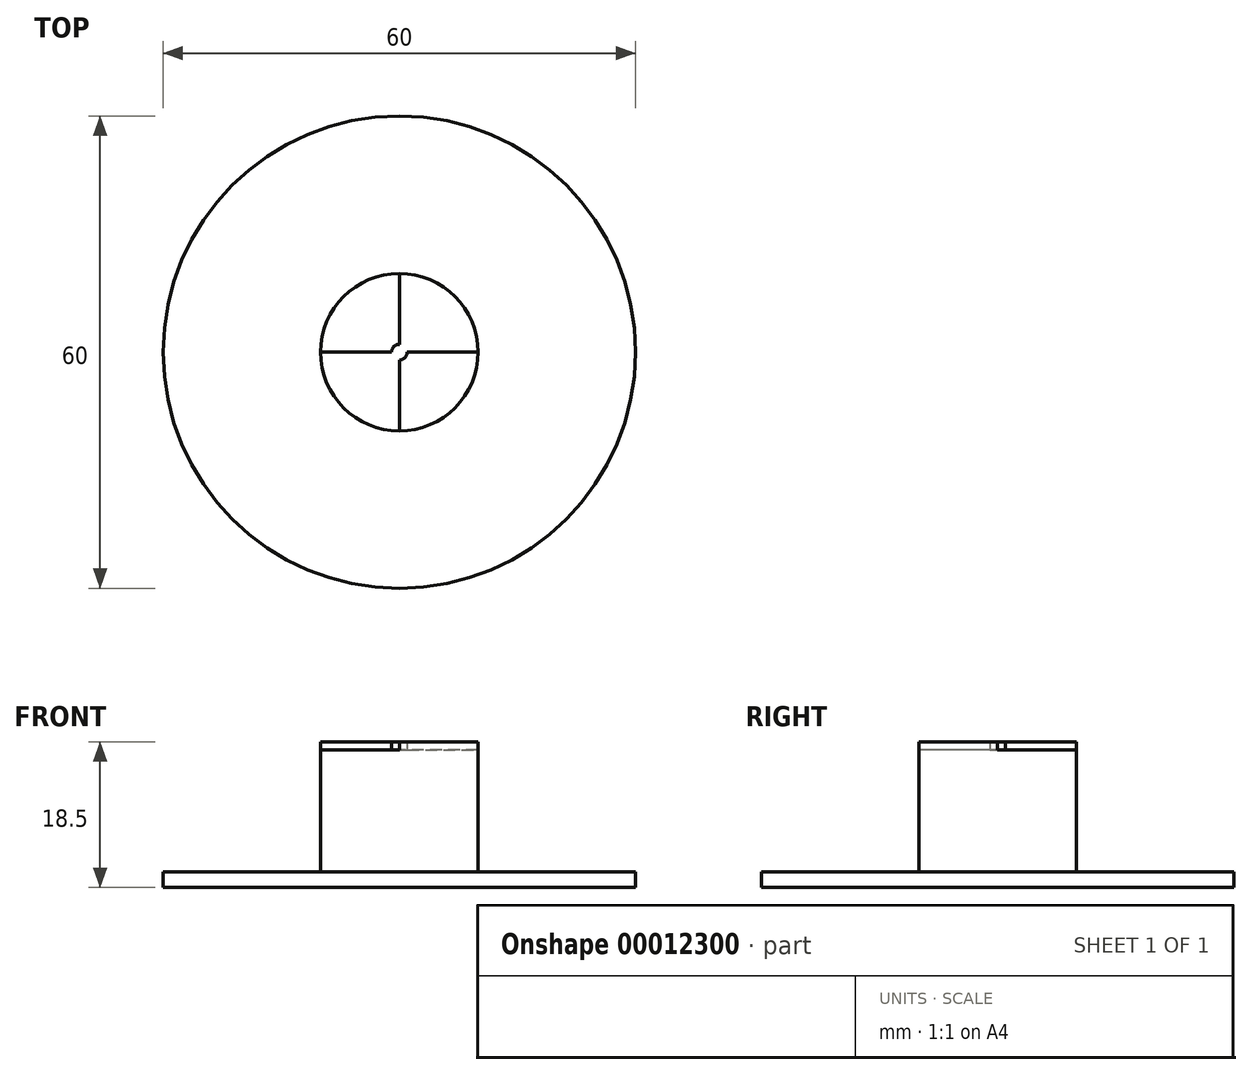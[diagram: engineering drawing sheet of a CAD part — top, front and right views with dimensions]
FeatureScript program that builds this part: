
annotation { "Feature Type Name" : "Feature", "Feature Type Description" : "" }
export const myFeature = defineFeature(function(context is Context, id is Id, definition is map)
    precondition{}
    {
        {
            var Q0;
            Q0=qCreatedBy(makeId("Top.planeOp"),FACE);
            var sketch = newSketch(context, id + "F0", { "sketchPlane" : qUnion([Q0])});
            skCircle(sketch, "E0", {"center": v(0, 0) * mm, "radius": 30 * mm});
            skSolve(sketch);
        }
        {
            var Q0;
            Q0=makeQuery(id+"F0.imprint","IMPRINT",FACE,{"disambiguationData":[TD([[makeQuery(id+"F0.imprint","IMPRINT",EDGE,{"derivedFrom":sQuery(id+"F0.wireOp",EDGE,"E0")}),1.0]])]});
            extrude(context, id + "F1", {"entities" : qUnion([Q0]), "depth" : 2 * mm});
        }
        {
            var Q0;
            Q0=makeQuery(id+"F1.opExtrude","CAP_FACE",FACE,{"disambiguationData":[OSD([sQuery(id+"F0.wireOp",EDGE,"E0")])],"isStart":false});
            var sketch = newSketch(context, id + "F2", { "sketchPlane" : qUnion([Q0])});
            skCircle(sketch, "E1", {"center": v(0, 0) * mm, "radius": 10 * mm});
            skSolve(sketch);
        }
        {
            var Q0;
            Q0=makeQuery(id+"F2.imprint","IMPRINT",FACE,{"disambiguationData":[TD([[makeQuery(id+"F2.imprint","IMPRINT",EDGE,{"derivedFrom":sQuery(id+"F2.wireOp",EDGE,"E1")}),1.0]])]});
            extrude(context, id + "F3", {"entities" : qUnion([Q0]), "operationType" : NewBodyOperationType.ADD, "depth" : 15.5 * mm});
        }
        {
            var Q0;
            Q0=makeQuery(id+"F3.opExtrude","CAP_FACE",FACE,{"disambiguationData":[OSD([sQuery(id+"F2.wireOp",EDGE,"E1")])],"isStart":false});
            var sketch = newSketch(context, id + "F4", { "sketchPlane" : qUnion([Q0])});
            skLineSegment(sketch, "E2", {"start": v(0, 0) * mm, "end": v(0, 10) * mm});
            skLineSegment(sketch, "E3", {"start": v(0, 0) * mm, "end": v(0, -10) * mm});
            skLineSegment(sketch, "E4", {"start": v(-10, 0) * mm, "end": v(10, 0) * mm});
            skCircle(sketch, "E5", {"center": v(0, 0) * mm, "radius": 1 * mm});
            skSolve(sketch);
        }
        {
            var Q0;
            {var subQ0=makeQuery(id+"F3.opExtrude","CAP_EDGE",EDGE,{"disambiguationData":[OSD([sQuery(id+"F2.wireOp",EDGE,"E1")])],"isStart":false});var subQ3=sQuery(id+"F4.wireOp",EDGE,"E3");var subQ4=makeQuery(id+"F4.imprint","INTERSECT",VERTEX,{"derivedFrom":[subQ0,subQ3]});Q0=makeQuery(id+"F4.imprint","IMPRINT",FACE,{"disambiguationData":[TD([[makeQuery(id+"F4.imprint","IMPRINT",EDGE,{"disambiguationData":[TD([[subQ4,1.0]])],"derivedFrom":subQ3}),1.0]])]});}
            extrude(context, id + "F5", {"entities" : qUnion([Q0]), "operationType" : NewBodyOperationType.ADD, "depth" : 1 * mm});
        }
        {
            var Q0;
            {var subQ0=makeQuery(id+"F3.opExtrude","CAP_EDGE",EDGE,{"disambiguationData":[OSD([sQuery(id+"F2.wireOp",EDGE,"E1")])],"isStart":false});var subQ3=sQuery(id+"F4.wireOp",EDGE,"E2");var subQ4=makeQuery(id+"F4.imprint","INTERSECT",VERTEX,{"derivedFrom":[subQ0,subQ3]});Q0=makeQuery(id+"F4.imprint","IMPRINT",FACE,{"disambiguationData":[TD([[makeQuery(id+"F4.imprint","IMPRINT",EDGE,{"disambiguationData":[TD([[subQ4,1.0]])],"derivedFrom":subQ3}),1.0]])]});}
            extrude(context, id + "F6", {"entities" : qUnion([Q0]), "operationType" : NewBodyOperationType.ADD, "depth" : 1 * mm});
        }
    });
